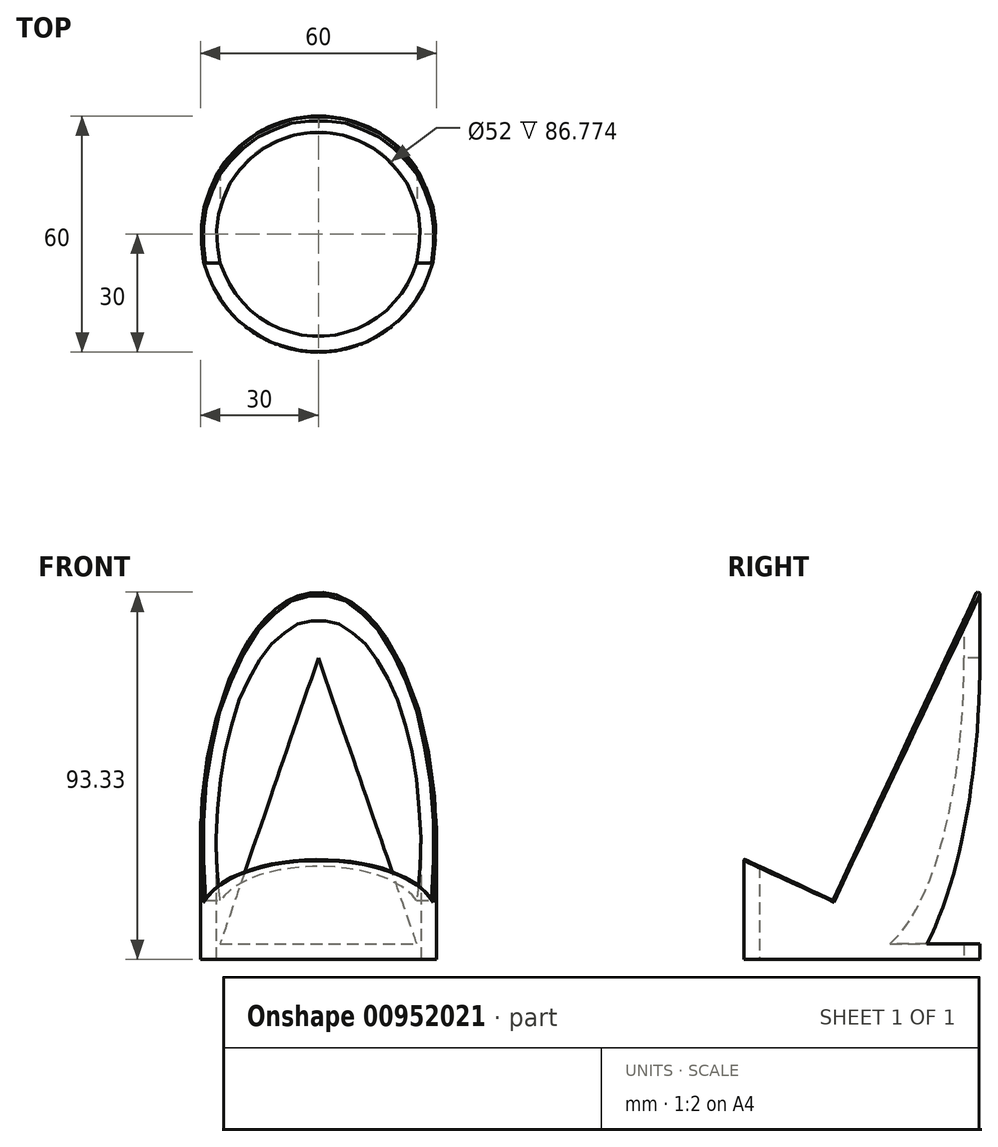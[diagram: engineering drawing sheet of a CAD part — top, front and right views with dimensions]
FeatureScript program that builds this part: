
annotation { "Feature Type Name" : "Feature", "Feature Type Description" : "" }
export const myFeature = defineFeature(function(context is Context, id is Id, definition is map)
    precondition{}
    {
        {
            var Q0;
            Q0=qCreatedBy(makeId("Top.planeOp"),FACE);
            var sketch = newSketch(context, id + "F0", { "sketchPlane" : qUnion([Q0])});
            skCircle(sketch, "E0", {"center": v(0, 0) * mm, "radius": 30 * mm});
            skCircle(sketch, "E1", {"center": v(0, 0) * mm, "radius": 26 * mm});
            skSolve(sketch);
        }
        {
            var Q0;
            Q0 = qSketchRegion(id + "F0", true);
            extrude(context, id + "F1", {"entities" : qUnion([Q0]), "depth" : 100 * mm, "offsetDistance" : 25 * mm});
        }
        {
            var Q0;
            Q0=qCreatedBy(makeId("Right.planeOp"),FACE);
            var sketch = newSketch(context, id + "F2", { "sketchPlane" : qUnion([Q0])});
            skLineSegment(sketch, "E2", {"start": v(-32.72, 26.83) * mm, "end": v(-7.34, 15) * mm});
            skLineSegment(sketch, "E3", {"start": v(-7.34, 15) * mm, "end": v(34.07, 103.82) * mm});
            skLineSegment(sketch, "E4", {"start": v(34.07, 103.82) * mm, "end": v(8.7, 115.65) * mm});
            skLineSegment(sketch, "E5", {"start": v(8.7, 115.65) * mm, "end": v(-32.72, 26.83) * mm, "construction": true});
            skLineSegment(sketch, "E6", {"start": v(-50.7, 0) * mm, "end": v(-50.7, 77.6) * mm, "construction": true});
            skLineSegment(sketch, "E7", {"start": v(8.7, 115.65) * mm, "end": v(-18.88, 128.51) * mm});
            skLineSegment(sketch, "E8", {"start": v(-18.88, 128.51) * mm, "end": v(-60.3, 39.7) * mm});
            skLineSegment(sketch, "E9", {"start": v(-60.3, 39.7) * mm, "end": v(-32.72, 26.83) * mm});
            skSolve(sketch);
        }
        {
            var Q0;
            Q0 = qSketchRegion(id + "F2", true);
            extrude(context, id + "F3", {"entities" : qUnion([Q0]), "operationType" : NewBodyOperationType.REMOVE, "oppositeDirection" : true, "depth" : 45 * mm, "offsetDistance" : 25 * mm, "hasSecondDirection" : true, "secondDirectionOppositeDirection" : false, "secondDirectionDepth" : 45 * mm});
        }
        {
            var Q0;
            Q0=qCreatedBy(makeId("Front.planeOp"),FACE);
            var sketch = newSketch(context, id + "F4", { "sketchPlane" : qUnion([Q0])});
            skLineSegment(sketch, "E10", {"start": v(25, 4) * mm, "end": v(0, 76.6) * mm});
            skLineSegment(sketch, "E11", {"start": v(0, 76.6) * mm, "end": v(-25, 4) * mm});
            skLineSegment(sketch, "E12", {"start": v(-25, 4) * mm, "end": v(25, 4) * mm});
            skSolve(sketch);
        }
        {
            var Q0;
            Q0=makeQuery(id+"F4.imprint","IMPRINT",FACE,{"disambiguationData":[TD([[makeQuery(id+"F4.imprint","IMPRINT",EDGE,{"derivedFrom":sQuery(id+"F4.wireOp",EDGE,"E10")}),1.0]])]});
            extrude(context, id + "F5", {"entities" : qUnion([Q0]), "operationType" : NewBodyOperationType.REMOVE, "oppositeDirection" : true, "depth" : 50 * mm, "offsetDistance" : 25 * mm});
        }
        {
            var Q0;
            Q0=makeQuery(id+"F3.boolean.opBoolean","INTERSECT",EDGE,{"derivedFrom":[makeQuery(id+"F1.opExtrude","SWEPT_FACE",FACE,{"disambiguationData":[OSD([sQuery(id+"F0.wireOp",EDGE,"E0")])]}),makeQuery(id+"F3.opExtrude","SWEPT_FACE",FACE,{"disambiguationData":[OSD([sQuery(id+"F2.wireOp",EDGE,"E3")])]})]});
            fillet(context, id + "F6", {"entities" : qUnion([Q0]), "radius" : 0.5 * mm, "tangentPropagation" : true, "allowEdgeOverflow" : false});
        }
        {
            var Q0;
            Q0=makeQuery(id+"F3.boolean.opBoolean","INTERSECT",EDGE,{"derivedFrom":[makeQuery(id+"F1.opExtrude","SWEPT_FACE",FACE,{"disambiguationData":[OSD([sQuery(id+"F0.wireOp",EDGE,"E0")])]}),makeQuery(id+"F3.opExtrude","SWEPT_FACE",FACE,{"disambiguationData":[OSD([sQuery(id+"F2.wireOp",EDGE,"E2"),sQuery(id+"F2.wireOp",EDGE,"E9")])]})]});
            fillet(context, id + "F7", {"entities" : qUnion([Q0]), "radius" : 0.25 * mm, "tangentPropagation" : true, "allowEdgeOverflow" : false});
        }
    });
